# Revit family: RX300
name_source: partatom
category: Apparecchi idraulici
units: mm (PartAtom-declared; Revit-internal decimal feet)

## family parameters
Basato su piano di lavoro = No
Condiviso = No
Mantieni orientamento annotazione = No
Numero OmniClass = 23.45.55.14
Punto di calcolo locali = No
Quota connettore circolare = Usa diametro
Sempre verticale = Sì
Taglio con vuoti quando caricato = No
Tipo di parte = Normale
Titolo OmniClass = Single Faucets

## types (12) — shared parameters
Cold water finishes = 10 mm  [stored 0.0328084 ft]
Commenti sul tipo = Exposed parts for manual wall hydroprogressive mixer
Connessione CW = No
Connessione HW = No
Connessione di scarico = No
Connessione di ventilazione = No
Descrizione = Exposed parts for manual wall hydroprogressive mixer
Hot water inlet = 10 mm  [stored 0.0328084 ft]
Produttore = IB Rubinetterie S.p.A.
URL = https://www.weareib.it
zero-valued in all types: Prospetto di default

## per-type parameters (varying)
| type | Finishes surface | Immagine tipo | Modello |
| Chrome | IB_Chrome | RX300CC.jpg | RX300CC |
| Black Chrome | IB_Black chrome | RX300CF.jpg | RX300CF |
| Brushed Black Chrome | IB_Brushed black chrome | RX300CS.jpg | RX300CS |
| Pale Gold | IB_Pale gold | RX300II.jpg | RX300II |
| Brushed Pale Gold | IB_brushed pale gold | RX300IS.jpg | RX300IS |
| Matt Black | IB_matt black | RX300NP.jpg | RX300NP |
| Natural Brass | IB_Brass | RX300ON.jpg | RX300ON |
| Gold | IB_gold | RX300OO.jpg | RX300OO |
| Brushed Gold | IB_brushed gold | RX300OS.jpg | RX300OS |
| Rose Gold | IB_Rose gold | RX300RS.jpg | RX300RS |
| Brushed Rose Gold | IB_Brushed rose gold | RX300SR.jpg | RX300SR |
| Brushed Nickel | IB_Brushed nickel | RX300SS.jpg | RX300SS |

note: [stored X ft] marks values corroborated as IEEE doubles in the binary element streams (Revit-internal decimal feet)
